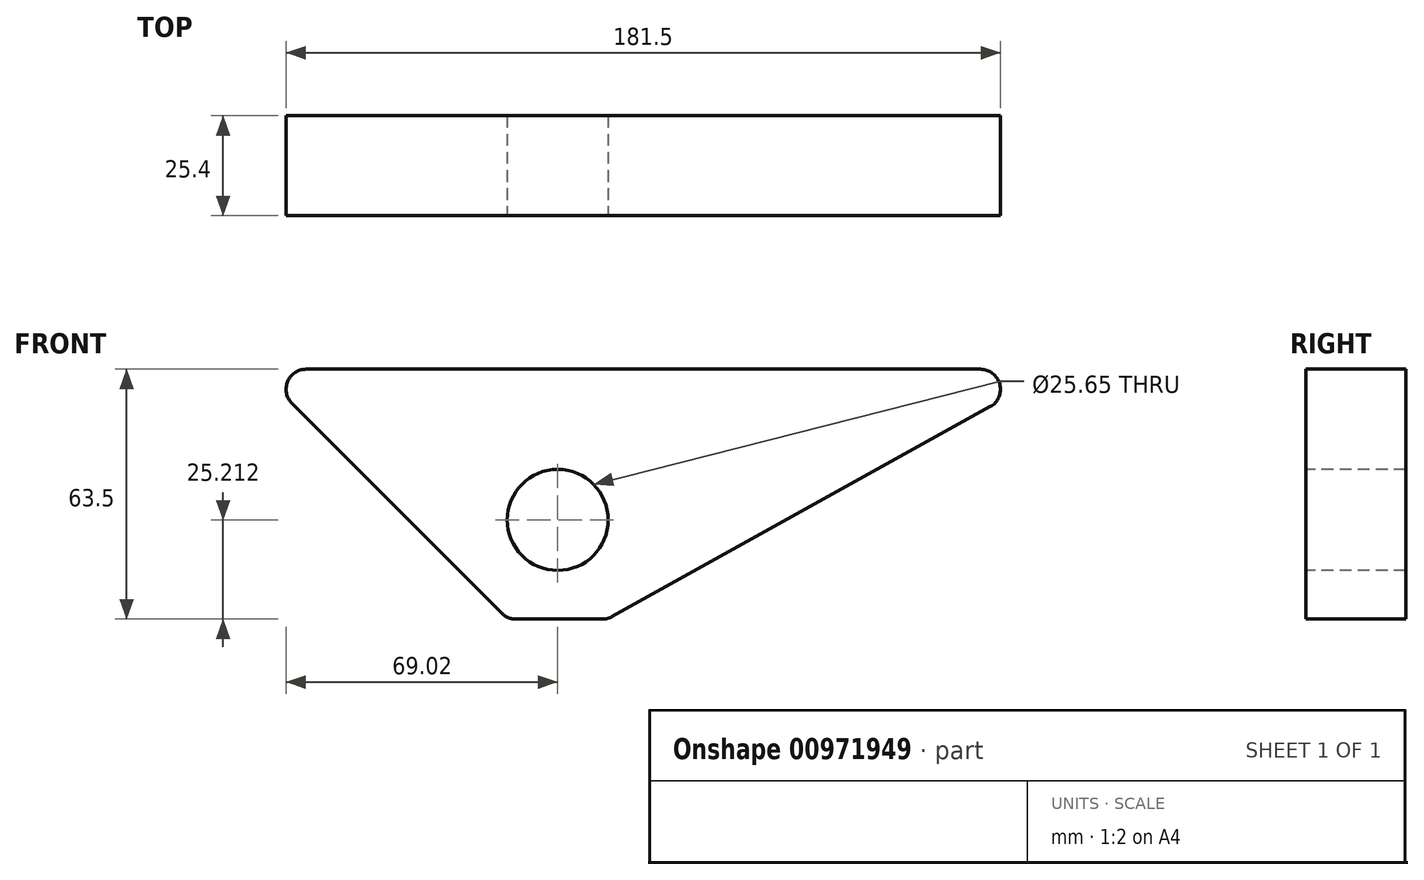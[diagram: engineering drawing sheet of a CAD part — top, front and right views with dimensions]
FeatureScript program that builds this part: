
annotation { "Feature Type Name" : "Feature", "Feature Type Description" : "" }
export const myFeature = defineFeature(function(context is Context, id is Id, definition is map)
    precondition{}
    {
        {
            var Q0;
            Q0=qCreatedBy(makeId("Front.planeOp"),FACE);
            var sketch = newSketch(context, id + "F0", { "sketchPlane" : qUnion([Q0])});
            skLineSegment(sketch, "E0", {"start": v(0, -16.68) * mm, "end": v(0, 46.82) * mm});
            skLineSegment(sketch, "E1", {"start": v(0, -16.68) * mm, "end": v(12.7, -16.68) * mm});
            skLineSegment(sketch, "E2", {"start": v(12.7, -16.68) * mm, "end": v(-12.7, -16.68) * mm});
            skLineSegment(sketch, "E3", {"start": v(0, 46.82) * mm, "end": v(-76.2, 46.82) * mm});
            skLineSegment(sketch, "E4", {"start": v(-76.2, 46.82) * mm, "end": v(-12.7, -16.68) * mm});
            skLineSegment(sketch, "E5", {"start": v(0, 46.82) * mm, "end": v(127, 46.82) * mm});
            skLineSegment(sketch, "E6", {"start": v(127, 46.82) * mm, "end": v(12.7, -16.68) * mm});
            skSolve(sketch);
        }
        {
            var Q0;
            {var subQ0=sQuery(id+"F0.wireOp",EDGE,"E0");Q0=makeQuery(id+"F0.imprint","IMPRINT",FACE,{"disambiguationData":[TD([[makeQuery(id+"F0.imprint","IMPRINT",EDGE,{"derivedFrom":subQ0}),1.0]])]});}
            var sketch = newSketch(context, id + "F1", { "sketchPlane" : qUnion([Q0])});
            skLineSegment(sketch, "E7", {"start": v(0, -16.87) * mm, "end": v(0, 8.53) * mm});
            skCircle(sketch, "E8", {"center": v(0, 8.53) * mm, "radius": 12.7 * mm});
            skSolve(sketch);
        }
        {
            var Q0;
            {var subQ0=sQuery(id+"F0.wireOp",EDGE,"E0");Q0=makeQuery(id+"F0.imprint","IMPRINT",FACE,{"disambiguationData":[TD([[makeQuery(id+"F0.imprint","IMPRINT",EDGE,{"derivedFrom":subQ0}),1.0]])]});}
            var Q1;
            {var subQ0=sQuery(id+"F0.wireOp",EDGE,"E0");Q1=makeQuery(id+"F0.imprint","IMPRINT",FACE,{"disambiguationData":[TD([[makeQuery(id+"F0.imprint","IMPRINT",EDGE,{"derivedFrom":subQ0}),-1.0]])]});}
            extrude(context, id + "F2", {"entities" : qUnion([Q0, Q1]), "depth" : 25.4 * mm, "offsetDistance" : 25.4 * mm});
        }
        {
            var Q0;
            {var subQ0=sQuery(id+"F1.wireOp",EDGE,"E7");var subQ1=makeQuery(id+"F0.imprint","IMPRINT",EDGE,{"derivedFrom":sQuery(id+"F0.wireOp",EDGE,"E0")});var subQ2=makeQuery(id+"F1.imprint","INTERSECT",VERTEX,{"derivedFrom":[subQ1,subQ0]});Q0=makeQuery(id+"F1.imprint","IMPRINT",FACE,{"disambiguationData":[TD([[makeQuery(id+"F1.imprint","IMPRINT",EDGE,{"disambiguationData":[TD([[subQ2,1.0]])],"derivedFrom":subQ0}),-1.0]])]});}
            var Q1;
            {var subQ0=sQuery(id+"F1.wireOp",EDGE,"E7");var subQ1=makeQuery(id+"F0.imprint","IMPRINT",EDGE,{"derivedFrom":sQuery(id+"F0.wireOp",EDGE,"E0")});var subQ2=makeQuery(id+"F1.imprint","INTERSECT",VERTEX,{"derivedFrom":[subQ1,subQ0]});Q1=makeQuery(id+"F1.imprint","IMPRINT",FACE,{"disambiguationData":[TD([[makeQuery(id+"F1.imprint","IMPRINT",EDGE,{"disambiguationData":[TD([[subQ2,1.0]])],"derivedFrom":subQ0}),1.0]])]});}
            extrude(context, id + "F3", {"entities" : qUnion([Q0, Q1]), "operationType" : NewBodyOperationType.REMOVE, "depth" : 25.4 * mm, "offsetDistance" : 25.4 * mm});
        }
        {
            var Q0;
            Q0=makeQuery(id+"F2.opExtrude","SWEPT_EDGE",EDGE,{"disambiguationData":[OSD([sQuery(id+"F0.wireOp",EDGE,"E2"),sQuery(id+"F0.wireOp",EDGE,"E4")])]});
            var Q1;
            Q1=makeQuery(id+"F2.opExtrude","SWEPT_EDGE",EDGE,{"disambiguationData":[OSD([sQuery(id+"F0.wireOp",EDGE,"E2"),sQuery(id+"F0.wireOp",EDGE,"E6")])]});
            var Q2;
            Q2=makeQuery(id+"F2.opExtrude","SWEPT_EDGE",EDGE,{"disambiguationData":[OSD([sQuery(id+"F0.wireOp",EDGE,"E5"),sQuery(id+"F0.wireOp",EDGE,"E6")])]});
            var Q3;
            Q3=makeQuery(id+"F2.opExtrude","SWEPT_EDGE",EDGE,{"disambiguationData":[OSD([sQuery(id+"F0.wireOp",EDGE,"E3"),sQuery(id+"F0.wireOp",EDGE,"E4")])]});
            fillet(context, id + "F4", {"entities" : qUnion([Q0, Q1, Q2, Q3]), "radius" : 5.08 * mm, "tangentPropagation" : true, "allowEdgeOverflow" : false});
        }
        {
            var Q0;
            Q0=makeQuery(id+"F2.opExtrude","CAP_FACE",FACE,{"disambiguationData":[OSD([sQuery(id+"F0.wireOp",EDGE,"E2"),sQuery(id+"F0.wireOp",EDGE,"E3"),sQuery(id+"F0.wireOp",EDGE,"E4"),sQuery(id+"F0.wireOp",EDGE,"E5"),sQuery(id+"F0.wireOp",EDGE,"E6")])],"isStart":false});
            var sketch = newSketch(context, id + "F5", { "sketchPlane" : qUnion([Q0])});
            skCircle(sketch, "E9", {"center": v(0, 8.53) * mm, "radius": 12.83 * mm});
            skSolve(sketch);
        }
        {
            var Q0;
            Q0=makeQuery(id+"F5.imprint","IMPRINT",FACE,{"disambiguationData":[TD([[makeQuery(id+"F5.imprint","IMPRINT",EDGE,{"derivedFrom":sQuery(id+"F5.wireOp",EDGE,"E9")}),1.0]])]});
            extrude(context, id + "F6", {"entities" : qUnion([Q0]), "operationType" : NewBodyOperationType.REMOVE, "oppositeDirection" : true, "depth" : 25.4 * mm, "offsetDistance" : 25.4 * mm});
        }
    });
